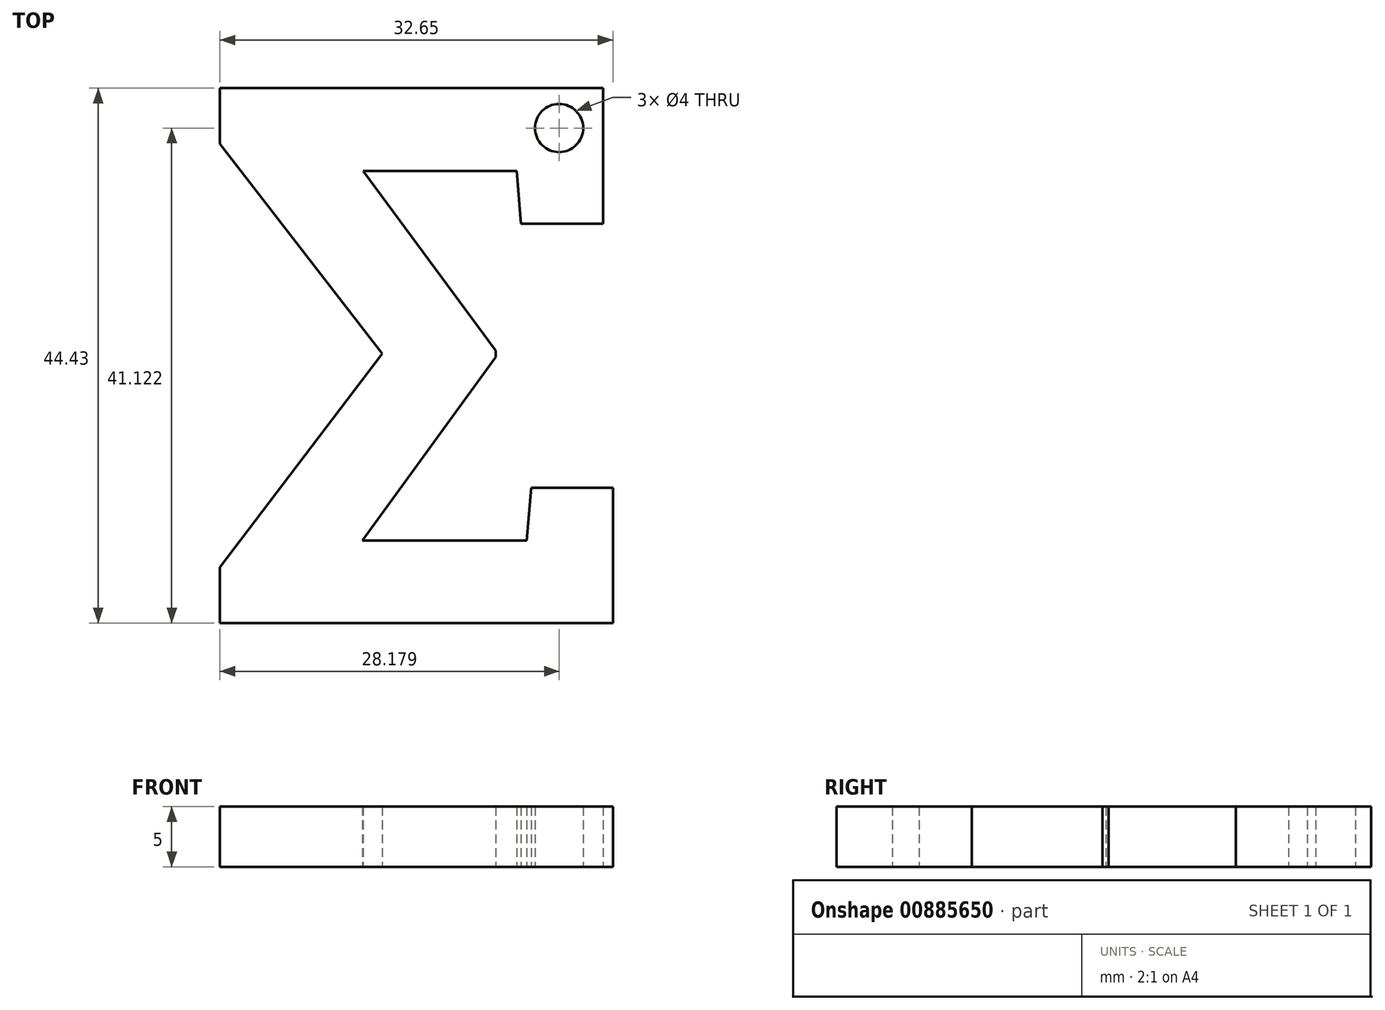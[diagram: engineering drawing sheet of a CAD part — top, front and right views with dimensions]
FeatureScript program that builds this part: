
annotation { "Feature Type Name" : "Feature", "Feature Type Description" : "" }
export const myFeature = defineFeature(function(context is Context, id is Id, definition is map)
    precondition{}
    {
        {
            var Q0;
            Q0=qCreatedBy(makeId("Top.planeOp"),FACE);
            var sketch = newSketch(context, id + "F0", { "sketchPlane" : qUnion([Q0])});
            skText(sketch, "E0", { "text": "Σ", "fontName": "RobotoSlab-Bold.ttf"});
            skCircle(sketch, "E1", {"center": v(-9.34, 27.06) * mm, "radius": 2 * mm});
            const initialGuessF0  = {"E0": [-0.03966, -0.01406, 1, 0, 0.045]};
            skSetInitialGuess(sketch, initialGuessF0);
            skSolve(sketch);
        }
        {
            var Q0;
            Q0=makeQuery(id+"F0.imprint","IMPRINT",FACE,{"disambiguationData":[TD([[makeQuery(id+"F0.imprint","IMPRINT",EDGE,{"derivedFrom":sQuery(id+"F0.wireOp",EDGE,"E0.sketch_text.stroke-0")}),-1.0]])]});
            extrude(context, id + "F1", {"entities" : qUnion([Q0]), "depth" : 5 * mm, "offsetDistance" : 25 * mm});
        }
    });
